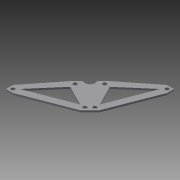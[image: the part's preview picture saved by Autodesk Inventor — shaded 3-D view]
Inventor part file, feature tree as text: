
AUTODESK INVENTOR PART (.ipt)
format: ipt  version: 2013 (Build 170138000, 138)  size: 111,616 bytes
history: native  units: in
note: dims shown in document units (in); Inventor stores cm internally (conversion verified against a paired STEP export)
features: extrude x1, sketch x1
ambient origin geometry x8: Origin, YZ Plane, XZ Plane, XY Plane, X Axis, Y Axis, Z Axis, Center Point
bodies: Solid1 (feature_tree)
feature tree (2):
  extrude  "Extrusion1"  Depth=0.266in
  sketch  "Sketch1"  dims[d4=0.75in d8=0.266in d9=0.266in d10=1.5in d12=0.75in d13=0.35in d14=0.35in d15=0.25in d17=0.25in d20=0.25in d21=0.25in d25=0.25in d26=0.5in d27=0.5in d28=0.125in d29=0.0in]
